# Revit family: Base_Cabinets-Teknion-RHBS_Standard_Base_Cabinet-R2018
name_source: partatom
category: Furniture
revit_build: Autodesk Revit 2018 (Build: 20190510_1515(x64)
units: mm (PartAtom-declared; Revit-internal decimal feet)

## family parameters
Always vertical = Yes
Cut with Voids When Loaded = No
OmniClass Number = 23.40.20.00
OmniClass Title = General Furniture and Specialties
Room Calculation Point = No
Shared = Yes
Work Plane-Based = No

## types (8) — shared parameters
Assembly Code = E2020200
Manufacturer = Teknion
Manufacturer Fax = 416.661.4586
Part Number = RHBS
Product Documentation Link = https://www.teknion.com
Product Line = Modular Cabinets
Product Page URL = https://www.teknion.com
Series = Modular Cabinets
Sustainability Data = https://www.teknion.com
URL = www.teknion.com
Unit Weight URL = http://www.teknion.com
Warranty = http://www.teknion.com

## per-type parameters (varying)
| type | Depth | Description | Doors | Height | Model | Shelf Height |
| With Doors, 24" Depth, 33" Height | 24 " | Standard Base Cabinet, With Doors, 24" Depth, 33" Height | Yes | 32.5 " | RHBSD24__33_ | 18.616 " |
| With Doors, 24" Depth, 35" Height | 24 " | Standard Base Cabinet, With Doors, 24" Depth, 35" Height | Yes | 35 " | RHBSD24__35_ | 19.866 " |
| With Doors, 29" Depth, 33" Height | 29 " | Standard Base Cabinet, With Doors, 29" Depth, 33" Height | Yes | 32.5 " | RHBSD29__33_ | 18.616 " |
| With Doors, 29" Depth, 35" Height | 29 " | Standard Base Cabinet, With Doors, 29" Depth, 35" Height | Yes | 35 " | RHBSD29__35_ | 19.866 " |
| No Doors, 24" Depth, 33" Height | 24 " | Standard Base Cabinet, No Doors, 24" Depth, 33" Height | No | 32.5 " | RHBSO24__33_ | 18.616 " |
| No Doors, 24" Depth, 35" Height | 24 " | Standard Base Cabinet, No Doors, 24" Depth, 35" Height | No | 35 " | RHBSO24__35_ | 19.866 " |
| No Doors, 29" Depth, 33" Height | 29 " | Standard Base Cabinet, No Doors, 29" Depth, 33" Height | No | 32.5 " | RHBSO29__33_ | 18.616 " |
| No Doors, 29" Depth, 35" Height | 29 " | Standard Base Cabinet, No Doors, 29" Depth, 35" Height | No | 35 " | RHBSO29__35_ | 19.866 " |

## geometry (parser evidence)
native form markers: Sweep x2
no freeform markers — native parametric forms only
